# Revit family: EKF_EE_ПанелиБоковыеДляСекционированияTrivia_AVERES
name_source: partatom
category: Электрооборудование
units: mm (PartAtom-declared; Revit-internal decimal feet)

## family parameters
Всегда вертикально = Нет
На основе рабочей плоскости = Да
Общий = Да
При загрузке вырезать с полостями = Нет
Размер круглого соединителя = Использовать диаметр
Тип детали = Силовой щит
Точка расчета площади = Нет

## types (14) — shared parameters
ADSK_Единица измерения = шт.
ADSK_Завод-изготовитель = EKF
ADSK_Количество = 1
ADSK_Материал = RAL 7035_Сталь
ADSK_Размер_Глубина = 1.5 мм
Глубина = 400 мм
Изготовитель = EKF
Отметка по умолчанию = 1219.2 мм
Серия номенклатуры = Averes
Степень защиты IP = -
ТВ = EKF_2_TRIVIA_AVERES
Тип установки = -
zero-valued in all types: ADSK_Масса

## per-type parameters (varying)
| type | ADSK_Код изделия | ADSK_Марка | ADSK_Наименование | ADSK_Обозначение | ADSK_Размер_Высота | ADSK_Размер_Ширина | Тип |
| Панели боковые для секционирования В600 Г600 мм (2шт) EKF AVERES | PCV66 | Панели боковые для секционирования В600 Г600 мм (2 шт) EKF AVERES | Панели боковые для секционирования В600 Г600 мм (2 шт) EKF AVERES | Панели боковые для секционирования В600 Г600 мм (2 шт) EKF AVERES | 607 мм | 516 мм | 711 мм |
| Панели боковые для секционирования В600 Г400 мм (2шт) EKF AVERES | PCV64 | Панели боковые для секционирования В600 Г400 мм (2 шт) EKF AVERES | Панели боковые для секционирования В600 Г400 мм (2 шт) EKF AVERES | Панели боковые для секционирования В600 Г400 мм (2 шт) EKF AVERES | 607 мм | 316 мм | 710 мм |
| Панели боковые для секционирования В500 Г600 мм (2шт) EKF AVERES | PCV56 | Панели боковые для секционирования В500 Г600 мм (2 шт) EKF AVERES | Панели боковые для секционирования В500 Г600 мм (2 шт) EKF AVERES | Панели боковые для секционирования В500 Г600 мм (2 шт) EKF AVERES | 507 мм | 516 мм | 709 мм |
| Панели боковые для секционирования В500 Г400 мм (2шт) EKF AVERES | PCV54 | Панели боковые для секционирования В500 Г400 мм (2 шт) EKF AVERES | Панели боковые для секционирования В500 Г400 мм (2 шт) EKF AVERES | Панели боковые для секционирования В500 Г400 мм (2 шт) EKF AVERES | 507 мм | 316 мм | 708 мм |
| Панели боковые для секционирования В400 Г600 мм (2шт) EKF AVERES | PCV46 | Панели боковые для секционирования В400 Г600 мм (2 шт) EKF AVERES | Панели боковые для секционирования В400 Г600 мм (2 шт) EKF AVERES | Панели боковые для секционирования В400 Г600 мм (2 шт) EKF AVERES | 407 мм | 516 мм | 707 мм |
| Панели боковые для секционирования В400 Г400 мм (2шт) EKF AVERES | PCV44 | Панели боковые для секционирования В400 Г400 мм (2 шт) EKF AVERES | Панели боковые для секционирования В400 Г400 мм (2 шт) EKF AVERES | Панели боковые для секционирования В400 Г400 мм (2 шт) EKF AVERES | 407 мм | 316 мм | 706 мм |
| Панели боковые для секционирования В300 Г600 мм (2шт) EKF AVERES | PCV36 | Панели боковые для секционирования В300 Г600 мм (2 шт) EKF AVERES | Панели боковые для секционирования В300 Г600 мм (2 шт) EKF AVERES | Панели боковые для секционирования В300 Г600 мм (2 шт) EKF AVERES | 307 мм | 516 мм | 705 мм |
| Панели боковые для секционирования В300 Г400 мм (2шт) EKF AVERES | PCV34 | Панели боковые для секционирования В300 Г400 мм (2 шт) EKF AVERES | Панели боковые для секционирования В300 Г400 мм (2 шт) EKF AVERES | Панели боковые для секционирования В300 Г400 мм (2 шт) EKF AVERES | 307 мм | 316 мм | 704 мм |
| Панели боковые для секционирования В200 Г600 мм (2шт) EKF AVERES | PCV26 | Панели боковые для секционирования В200 Г600 мм (2 шт) EKF AVERES | Панели боковые для секционирования В200 Г600 мм (2 шт) EKF AVERES | Панели боковые для секционирования В200 Г600 мм (2 шт) EKF AVERES | 207 мм | 516 мм | 703 мм |
| Панели боковые для секционирования В200 Г400 мм (2шт) EKF AVERES | PCV24 | Панели боковые для секционирования В200 Г400 мм (2 шт) EKF AVERES | Панели боковые для секционирования В200 Г400 мм (2 шт) EKF AVERES | Панели боковые для секционирования В200 Г400 мм (2 шт) EKF AVERES | 207 мм | 316 мм | 702 мм |
| Панели боковые для секционирования В150 Г600 мм (2шт) EKF AVERES | PCV156 | Панели боковые для секционирования В150 Г600 мм (2 шт) EKF AVERES | Панели боковые для секционирования В150 Г600 мм (2 шт) EKF AVERES | Панели боковые для секционирования В150 Г600 мм (2 шт) EKF AVERES | 157 мм | 516 мм | 701 мм |
| Панели боковые для секционирования В150 Г400 мм (2шт) EKF AVERES | PCV154 | Панели боковые для секционирования В150 Г400 мм (2 шт) EKF AVERES | Панели боковые для секционирования В150 Г400 мм (2 шт) EKF AVERES | Панели боковые для секционирования В150 Г400 мм (2 шт) EKF AVERES | 157 мм | 316 мм | 700 мм |
| Панели боковые для секционирования В100 Г600 мм (2шт) EKF AVERES | PCV16 | Панели боковые для секционирования В100 Г600 мм (2 шт) EKF AVERES | Панели боковые для секционирования В100 Г600 мм (2 шт) EKF AVERES | Панели боковые для секционирования В100 Г600 мм (2 шт) EKF AVERES | 107 мм | 516 мм | 699 мм |
| Панели боковые для секционирования В100 Г400 мм (2шт) EKF AVERES | PCV14 | Панели боковые для секционирования В100 Г400 мм (2 шт) EKF AVERES | Панели боковые для секционирования В100 Г400 мм (2 шт) EKF AVERES | Панели боковые для секционирования В100 Г400 мм (2 шт) EKF AVERES | 107 мм | 316 мм | 698 мм |
